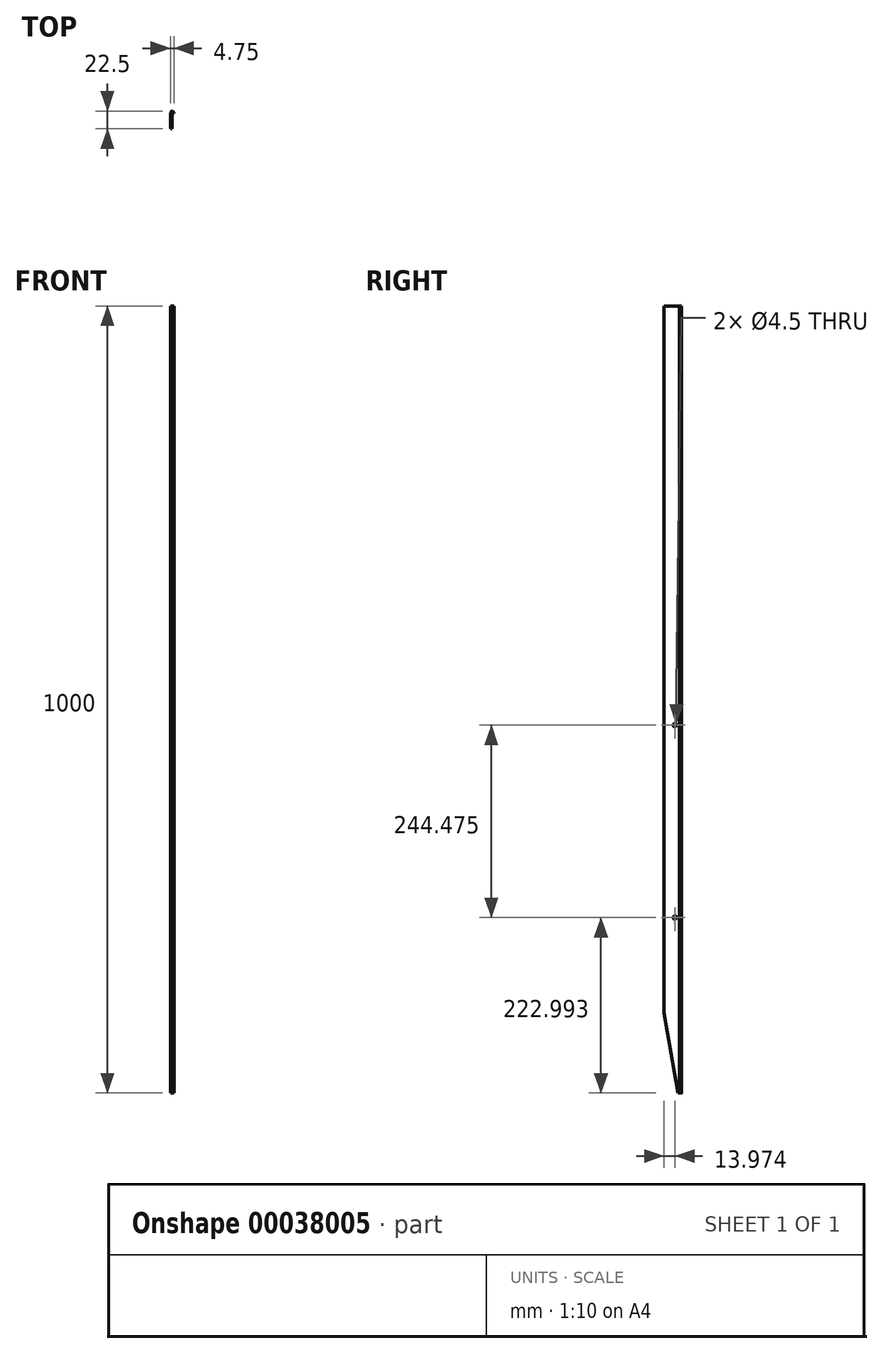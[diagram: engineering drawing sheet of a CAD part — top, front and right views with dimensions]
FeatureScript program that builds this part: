
annotation { "Feature Type Name" : "Feature", "Feature Type Description" : "" }
export const myFeature = defineFeature(function(context is Context, id is Id, definition is map)
    precondition{}
    {
        {
            var Q0;
            Q0=qCreatedBy(makeId("Top.planeOp"),FACE);
            var sketch = newSketch(context, id + "F0", { "sketchPlane" : qUnion([Q0])});
            skLineSegment(sketch, "E0.bottom", {"start": v(0, 0) * mm, "end": v(2.37, 0) * mm});
            skLineSegment(sketch, "E0.top", {"start": v(0, -19.53) * mm, "end": v(2.38, -19.53) * mm});
            skLineSegment(sketch, "E0.left", {"start": v(0, 0) * mm, "end": v(0, -19.53) * mm});
            skLineSegment(sketch, "E0.right", {"start": v(2.38, 0) * mm, "end": v(2.38, -19.53) * mm});
            skLineSegment(sketch, "E1", {"start": v(2.38, 0) * mm, "end": v(2.37, 2.97) * mm, "construction": true});
            skLineSegment(sketch, "E2", {"start": v(2.38, 0) * mm, "end": v(4.75, 0) * mm});
            skArc(sketch, "E3", {"start": v(2.94, 2.74) * mm, "mid": v(2.37, 2.97) * mm, "end": v(1.81, 2.74) * mm});
            skLineSegment(sketch, "E4", {"start": v(0, 0) * mm, "end": v(0, 0.92) * mm});
            skLineSegment(sketch, "E5", {"start": v(4.75, 0) * mm, "end": v(4.75, 0.92) * mm});
            skLineSegment(sketch, "E6", {"start": v(2.94, 2.74) * mm, "end": v(4.75, 0.92) * mm});
            skLineSegment(sketch, "E7", {"start": v(1.81, 2.74) * mm, "end": v(0, 0.92) * mm});
            skSolve(sketch);
        }
        {
            var Q0;
            Q0=qSketchRegion(id+"F0",true);
            extrude(context, id + "F1", {"entities" : qUnion([Q0]), "depth" : 1000 * mm});
        }
        {
            var Q0;
            Q0=makeQuery(id+"F1.opExtrude","SWEPT_FACE",FACE,{"disambiguationData":[OSD([sQuery(id+"F0.wireOp",EDGE,"E0.left"),sQuery(id+"F0.wireOp",EDGE,"E4")])]});
            var sketch = newSketch(context, id + "F2", { "sketchPlane" : qUnion([Q0])});
            skLineSegment(sketch, "E8.bottom", {"start": v(19.53, 0) * mm, "end": v(1.59, 0) * mm});
            skLineSegment(sketch, "E8.top", {"start": v(19.53, 101.75) * mm, "end": v(1.59, 101.75) * mm, "construction": true});
            skLineSegment(sketch, "E8.left", {"start": v(19.53, 0) * mm, "end": v(19.53, 101.75) * mm});
            skLineSegment(sketch, "E8.right", {"start": v(1.59, 0) * mm, "end": v(1.59, 101.75) * mm, "construction": true});
            skLineSegment(sketch, "E9", {"start": v(19.53, 101.75) * mm, "end": v(1.59, 0) * mm});
            skLineSegment(sketch, "E10", {"start": v(5.56, 101.75) * mm, "end": v(5.56, 223) * mm, "construction": true});
            skCircle(sketch, "E11", {"center": v(5.56, 223) * mm, "radius": 2.25 * mm});
            skLineSegment(sketch, "E12", {"start": v(5.56, 223) * mm, "end": v(5.56, 467.47) * mm, "construction": true});
            skCircle(sketch, "E13", {"center": v(5.56, 467.47) * mm, "radius": 2.25 * mm});
            skSolve(sketch);
        }
        {
            var Q0;
            Q0=qSketchRegion(id+"F2",true);
            var Q1;
            Q1=makeQuery(id+"F1.opExtrude","SWEPT_FACE",FACE,{"disambiguationData":[OSD([sQuery(id+"F0.wireOp",EDGE,"E5")])]});
            extrude(context, id + "F3", {"entities" : qUnion([Q0]), "operationType" : NewBodyOperationType.REMOVE, "endBound" : BoundingType.UP_TO_SURFACE, "oppositeDirection" : true, "endBoundEntityFace" : qUnion([Q1]), "depth" : 25.4 * mm});
        }
    });
